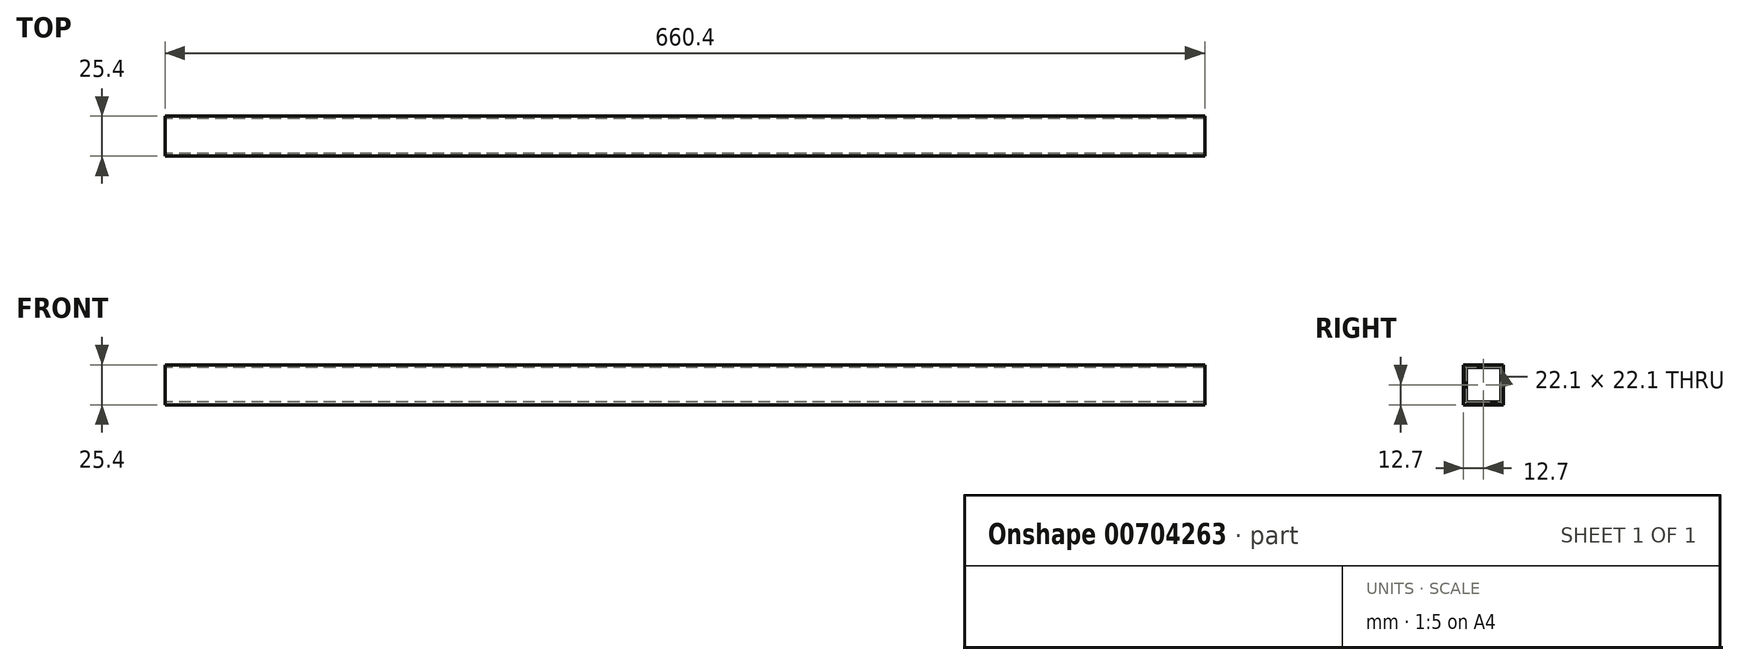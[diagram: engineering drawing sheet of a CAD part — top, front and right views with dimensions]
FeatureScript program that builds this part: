
annotation { "Feature Type Name" : "Feature", "Feature Type Description" : "" }
export const myFeature = defineFeature(function(context is Context, id is Id, definition is map)
    precondition{}
    {
        {
            var Q0;
            Q0=qCreatedBy(makeId("Front.planeOp"),FACE);
            var sketch = newSketch(context, id + "F0", { "sketchPlane" : qUnion([Q0])});
            skLineSegment(sketch, "E0.bottom", {"start": v(-330.2, 12.7) * mm, "end": v(330.2, 12.7) * mm});
            skLineSegment(sketch, "E0.top", {"start": v(-330.2, -12.7) * mm, "end": v(330.2, -12.7) * mm});
            skLineSegment(sketch, "E0.left", {"start": v(-330.2, 12.7) * mm, "end": v(-330.2, -12.7) * mm});
            skLineSegment(sketch, "E0.right", {"start": v(330.2, 12.7) * mm, "end": v(330.2, -12.7) * mm});
            skPoint(sketch, "E0.middle", {"position": v(0, 0) * mm});
            skSolve(sketch);
        }
        {
            var Q0;
            Q0 = qSketchRegion(id + "F0", true);
            extrude(context, id + "F1", {"entities" : qUnion([Q0]), "endBound" : BoundingType.SYMMETRIC, "depth" : 25.4 * mm, "offsetDistance" : 25.4 * mm});
        }
        {
            var Q0;
            Q0=qCreatedBy(makeId("Right.planeOp"),FACE);
            var sketch = newSketch(context, id + "F2", { "sketchPlane" : qUnion([Q0])});
            skLineSegment(sketch, "E1.bottom", {"start": v(11.05, 11.05) * mm, "end": v(-11.05, 11.05) * mm});
            skLineSegment(sketch, "E1.top", {"start": v(11.05, -11.05) * mm, "end": v(-11.05, -11.05) * mm});
            skLineSegment(sketch, "E1.left", {"start": v(11.05, 11.05) * mm, "end": v(11.05, -11.05) * mm});
            skLineSegment(sketch, "E1.right", {"start": v(-11.05, 11.05) * mm, "end": v(-11.05, -11.05) * mm});
            skPoint(sketch, "E1.middle", {"position": v(0, 0) * mm});
            skSolve(sketch);
        }
        {
            var Q0;
            Q0=makeQuery(id+"F2.imprint","IMPRINT",FACE,{"disambiguationData":[TD([[makeQuery(id+"F2.imprint","IMPRINT",EDGE,{"derivedFrom":sQuery(id+"F2.wireOp",EDGE,"E1.bottom")}),1.0]])]});
            extrude(context, id + "F3", {"entities" : qUnion([Q0]), "operationType" : NewBodyOperationType.REMOVE, "endBound" : BoundingType.SYMMETRIC, "depth" : 660.4 * mm, "offsetDistance" : 25.4 * mm});
        }
    });
